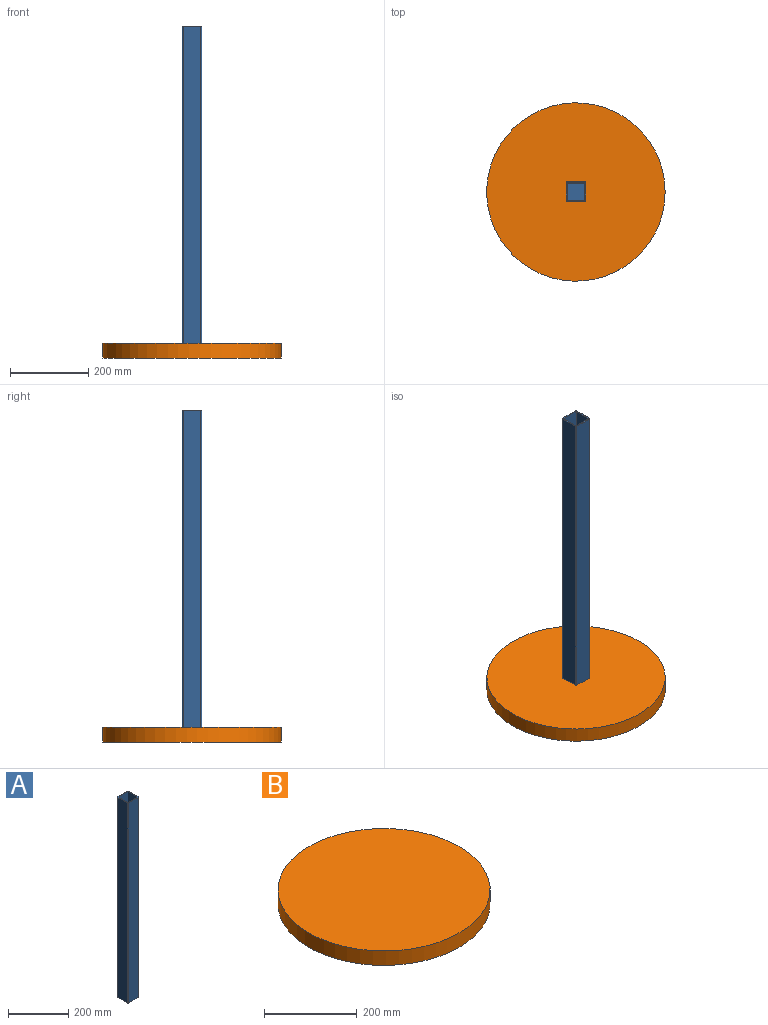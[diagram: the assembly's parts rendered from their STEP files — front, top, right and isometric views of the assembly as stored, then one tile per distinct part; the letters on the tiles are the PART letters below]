
ASSEMBLY  parts=2 mates=1
PART A: 15 faces, bbox 50.8x50.8x812.8 mm
  f0: cylinder r=3.17mm len=812.8mm, axis (0,0,-1), area 4053.7mm2, adj f1,f7,f8,f9
  f1: plane 812.8x44.45mm, normal (0,-1,0), area 36129mm2, adj f0,f2,f8,f9
  f2: cylinder r=3.17mm len=812.8mm, axis (0,0,-1), area 4053.7mm2, adj f1,f3,f8,f9
  f3: plane 812.8x44.45mm, normal (1,0,0), area 36129mm2, adj f2,f4,f8,f9
  f4: cylinder r=3.17mm len=812.8mm, axis (0,0,-1), area 4053.7mm2, adj f3,f5,f8,f9
  f5: plane 812.8x44.45mm, normal (0,1,0), area 36129mm2, adj f4,f6,f8,f9
  f6: cylinder r=3.17mm len=812.8mm, axis (0,0,-1), area 4053.7mm2, adj f5,f7,f8,f9
  f7: plane 812.8x44.45mm, normal (-1,0,0), area 36129mm2, adj f0,f6,f8,f9
  f8: plane 50.8x50.8mm, normal (0,0,1), area 596.2mm2, adj f0,f1,f2,f3,f4,f5,f6,f7
  f9: plane 50.8x50.8mm, normal (0,0,-1), area 2572mm2, adj f0,f1,f2,f3,f4,f5,f6,f7
  f10: plane 809.63x44.45mm, normal (0,1,0), area 35987.8mm2, adj f8,f11,f13,f14
  f11: plane 809.63x44.45mm, normal (-1,0,0), area 35987.8mm2, adj f8,f10,f12,f14
  f12: plane 809.63x44.45mm, normal (0,-1,0), area 35987.8mm2, adj f8,f11,f13,f14
  f13: plane 809.63x44.45mm, normal (1,0,0), area 35987.8mm2, adj f8,f10,f12,f14
  f14: plane 44.45x44.45mm, normal (0,0,1), area 1975.8mm2, adj f10,f11,f12,f13
PART B: 3 faces, bbox 457.2x457.2x38.1 mm
  f0: cylinder r=228.6mm len=457.2mm, axis (0,0,-1), area 54724.4mm2, adj f1,f2
  f1: plane 457.2x457.2mm, normal (0,0,1), area 164173.2mm2, adj f0
  f2: plane 457.2x457.2mm, normal (0,0,-1), area 164173.2mm2, adj f0
PLACE A t=(397.59,683.89,-120.1)mm
PLACE B t=(397.59,683.89,-158.2)mm
MATE planar B.f0 <-> A.f9  axis (0,0,1) through (397.59,683.89,-120.1)mm
